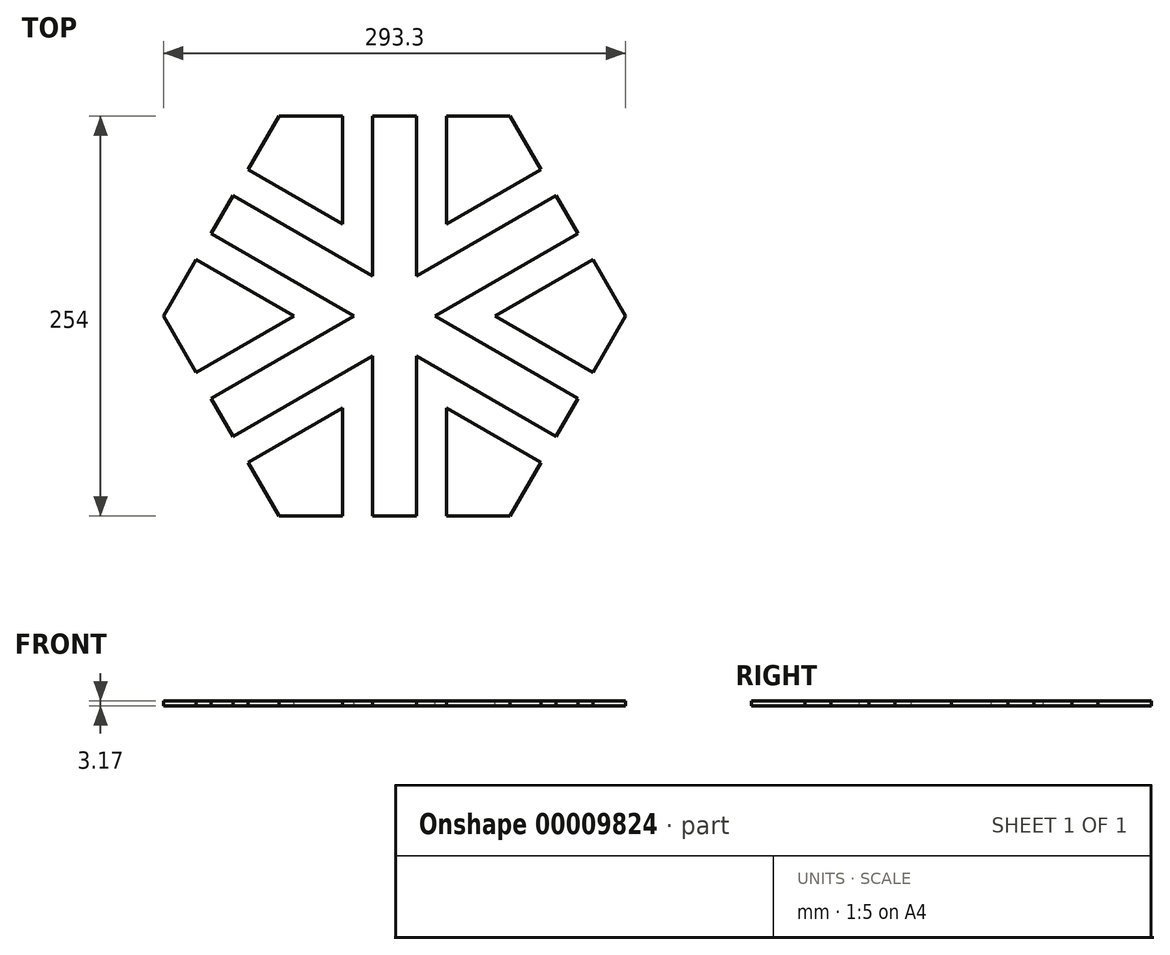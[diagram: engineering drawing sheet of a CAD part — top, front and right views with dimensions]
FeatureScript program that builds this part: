
annotation { "Feature Type Name" : "Feature", "Feature Type Description" : "" }
export const myFeature = defineFeature(function(context is Context, id is Id, definition is map)
    precondition{}
    {
        {
            var Q0;
            Q0=qCreatedBy(makeId("Top.planeOp"),FACE);
            var sketch = newSketch(context, id + "F0", { "sketchPlane" : qUnion([Q0])});
            skCircle(sketch, "E0.cCircle", {"center": v(0, 0) * mm, "radius": 127 * mm, "construction": true});
            skLineSegment(sketch, "E0.0", {"start": v(-73.32, 127) * mm, "end": v(73.32, 127) * mm});
            skLineSegment(sketch, "E0.1", {"start": v(73.32, 127) * mm, "end": v(146.65, 0) * mm});
            skLineSegment(sketch, "E0.2", {"start": v(146.65, 0) * mm, "end": v(73.32, -127) * mm});
            skLineSegment(sketch, "E0.3", {"start": v(73.32, -127) * mm, "end": v(-73.32, -127) * mm});
            skLineSegment(sketch, "E0.4", {"start": v(-73.32, -127) * mm, "end": v(-146.65, 0) * mm});
            skLineSegment(sketch, "E0.5", {"start": v(-146.65, 0) * mm, "end": v(-73.32, 127) * mm});
            skPoint(sketch, "E0.0.midPoint", {"position": v(0, 127) * mm});
            skSolve(sketch);
        }
        {
            var Q0;
            Q0=makeQuery(id+"F0.imprint","IMPRINT",FACE,{"disambiguationData":[TD([[makeQuery(id+"F0.imprint","IMPRINT",EDGE,{"derivedFrom":sQuery(id+"F0.wireOp",EDGE,"E0.0")}),-1.0]])]});
            extrude(context, id + "F1", {"entities" : qUnion([Q0]), "depth" : 3.17 * mm});
        }
        {
            var Q0;
            Q0=makeQuery(id+"F1.opExtrude","CAP_FACE",FACE,{"disambiguationData":[OSD([sQuery(id+"F0.wireOp",EDGE,"E0.0"),sQuery(id+"F0.wireOp",EDGE,"E0.1"),sQuery(id+"F0.wireOp",EDGE,"E0.2"),sQuery(id+"F0.wireOp",EDGE,"E0.3"),sQuery(id+"F0.wireOp",EDGE,"E0.4"),sQuery(id+"F0.wireOp",EDGE,"E0.5")])],"isStart":false});
            var sketch = newSketch(context, id + "F2", { "sketchPlane" : qUnion([Q0])});
            skLineSegment(sketch, "E1", {"start": v(13.97, 127) * mm, "end": v(13.97, 25.4) * mm});
            skLineSegment(sketch, "E2", {"start": v(33.02, 58.4) * mm, "end": v(33.02, 127) * mm});
            skLineSegment(sketch, "E3", {"start": v(13.97, 127) * mm, "end": v(33.02, 127) * mm});
            skLineSegment(sketch, "E4", {"start": v(-13.97, 127) * mm, "end": v(-13.97, 25.4) * mm});
            skLineSegment(sketch, "E5", {"start": v(-13.97, 25.4) * mm, "end": v(-33.02, 58.4) * mm});
            skLineSegment(sketch, "E6", {"start": v(-33.02, 58.4) * mm, "end": v(-33.02, 127) * mm});
            skLineSegment(sketch, "E7", {"start": v(-33.02, 127) * mm, "end": v(-13.97, 127) * mm});
            skPoint(sketch, "E8", {"position": v(0, 18.66) * mm});
            skLineSegment(sketch, "E9", {"start": v(-13.97, -127) * mm, "end": v(-13.97, -25.4) * mm});
            skLineSegment(sketch, "E10", {"start": v(13.97, -127) * mm, "end": v(13.97, -25.4) * mm});
            skLineSegment(sketch, "E11", {"start": v(-13.97, -25.4) * mm, "end": v(-33.02, -58.4) * mm});
            skLineSegment(sketch, "E12", {"start": v(13.97, -25.4) * mm, "end": v(33.02, -58.4) * mm});
            skLineSegment(sketch, "E13", {"start": v(-33.02, -127) * mm, "end": v(-33.02, -58.4) * mm});
            skLineSegment(sketch, "E14", {"start": v(33.02, -127) * mm, "end": v(33.02, -58.4) * mm});
            skLineSegment(sketch, "E15", {"start": v(33.02, -58.4) * mm, "end": v(92.95, -93) * mm});
            skLineSegment(sketch, "E16", {"start": v(13.97, -25.4) * mm, "end": v(102.48, -76.5) * mm});
            skLineSegment(sketch, "E17", {"start": v(-13.97, -25.4) * mm, "end": v(-102.48, -76.5) * mm});
            skLineSegment(sketch, "E18", {"start": v(-33.02, -58.4) * mm, "end": v(-92.95, -93) * mm});
            skLineSegment(sketch, "E19", {"start": v(-13.97, 25.4) * mm, "end": v(-102.48, 76.5) * mm});
            skLineSegment(sketch, "E20", {"start": v(-33.02, 58.4) * mm, "end": v(-92.95, 93) * mm});
            skLineSegment(sketch, "E21", {"start": v(-125.97, -35.8) * mm, "end": v(-63.96, 0) * mm});
            skLineSegment(sketch, "E22", {"start": v(-116.45, -52.3) * mm, "end": v(-25.86, 0) * mm});
            skLineSegment(sketch, "E23", {"start": v(-125.97, 35.8) * mm, "end": v(-63.96, 0) * mm});
            skLineSegment(sketch, "E24", {"start": v(-116.45, 52.3) * mm, "end": v(-25.86, 0) * mm});
            skLineSegment(sketch, "E25", {"start": v(-63.96, 0) * mm, "end": v(-25.86, 0) * mm});
            skLineSegment(sketch, "E26", {"start": v(125.97, -35.8) * mm, "end": v(63.96, 0) * mm});
            skLineSegment(sketch, "E27", {"start": v(116.45, -52.3) * mm, "end": v(25.86, 0) * mm});
            skLineSegment(sketch, "E28", {"start": v(125.97, 35.8) * mm, "end": v(63.96, 0) * mm});
            skLineSegment(sketch, "E29", {"start": v(116.45, 52.3) * mm, "end": v(25.86, 0) * mm});
            skLineSegment(sketch, "E30", {"start": v(25.86, 0) * mm, "end": v(63.96, 0) * mm});
            skLineSegment(sketch, "E31", {"start": v(13.97, 25.4) * mm, "end": v(33.02, 58.4) * mm});
            skLineSegment(sketch, "E32", {"start": v(33.02, 58.4) * mm, "end": v(92.95, 93) * mm});
            skLineSegment(sketch, "E33", {"start": v(13.97, 25.4) * mm, "end": v(102.48, 76.5) * mm});
            skSolve(sketch);
        }
        {
            var Q0;
            Q0=makeQuery(id+"F2.imprint","IMPRINT",FACE,{"disambiguationData":[TD([[makeQuery(id+"F2.imprint","IMPRINT",EDGE,{"derivedFrom":sQuery(id+"F2.wireOp",EDGE,"E4")}),-1.0]])]});
            var Q1;
            Q1=makeQuery(id+"F2.imprint","IMPRINT",FACE,{"disambiguationData":[TD([[makeQuery(id+"F2.imprint","IMPRINT",EDGE,{"derivedFrom":sQuery(id+"F2.wireOp",EDGE,"E1")}),1.0]])]});
            var Q2;
            Q2=makeQuery(id+"F2.imprint","IMPRINT",FACE,{"disambiguationData":[TD([[makeQuery(id+"F2.imprint","IMPRINT",EDGE,{"derivedFrom":sQuery(id+"F2.wireOp",EDGE,"97fdafe7-2def-440a-8930-caca40e22c30")}),-1.0]])]});
            var Q3;
            Q3=makeQuery(id+"F2.imprint","IMPRINT",FACE,{"disambiguationData":[TD([[makeQuery(id+"F2.imprint","IMPRINT",EDGE,{"derivedFrom":sQuery(id+"F2.wireOp",EDGE,"09cba625-7b20-47fa-ac99-ce42a038881a")}),1.0]])]});
            var Q4;
            Q4=makeQuery(id+"F2.imprint","IMPRINT",FACE,{"disambiguationData":[TD([[makeQuery(id+"F2.imprint","IMPRINT",EDGE,{"derivedFrom":sQuery(id+"F2.wireOp",EDGE,"E5")}),1.0]])]});
            var Q5;
            {var subQ2=sQuery(id+"F2.wireOp",EDGE,"E23");Q5=makeQuery(id+"F2.imprint","IMPRINT",FACE,{"disambiguationData":[TD([[makeQuery(id+"F2.imprint","IMPRINT",EDGE,{"derivedFrom":subQ2}),1.0]])]});}
            var Q6;
            {var subQ2=sQuery(id+"F2.wireOp",EDGE,"E21");Q6=makeQuery(id+"F2.imprint","IMPRINT",FACE,{"disambiguationData":[TD([[makeQuery(id+"F2.imprint","IMPRINT",EDGE,{"derivedFrom":subQ2}),-1.0]])]});}
            var Q7;
            Q7=makeQuery(id+"F2.imprint","IMPRINT",FACE,{"disambiguationData":[TD([[makeQuery(id+"F2.imprint","IMPRINT",EDGE,{"derivedFrom":sQuery(id+"F2.wireOp",EDGE,"E11")}),-1.0]])]});
            var Q8;
            {var subQ2=sQuery(id+"F2.wireOp",EDGE,"E9");Q8=makeQuery(id+"F2.imprint","IMPRINT",FACE,{"disambiguationData":[TD([[makeQuery(id+"F2.imprint","IMPRINT",EDGE,{"derivedFrom":subQ2}),1.0]])]});}
            var Q9;
            {var subQ2=sQuery(id+"F2.wireOp",EDGE,"E10");Q9=makeQuery(id+"F2.imprint","IMPRINT",FACE,{"disambiguationData":[TD([[makeQuery(id+"F2.imprint","IMPRINT",EDGE,{"derivedFrom":subQ2}),-1.0]])]});}
            var Q10;
            Q10=makeQuery(id+"F2.imprint","IMPRINT",FACE,{"disambiguationData":[TD([[makeQuery(id+"F2.imprint","IMPRINT",EDGE,{"derivedFrom":sQuery(id+"F2.wireOp",EDGE,"E12")}),1.0]])]});
            var Q11;
            {var subQ2=sQuery(id+"F2.wireOp",EDGE,"E26");Q11=makeQuery(id+"F2.imprint","IMPRINT",FACE,{"disambiguationData":[TD([[makeQuery(id+"F2.imprint","IMPRINT",EDGE,{"derivedFrom":subQ2}),1.0]])]});}
            var Q12;
            {var subQ2=sQuery(id+"F2.wireOp",EDGE,"E28");Q12=makeQuery(id+"F2.imprint","IMPRINT",FACE,{"disambiguationData":[TD([[makeQuery(id+"F2.imprint","IMPRINT",EDGE,{"derivedFrom":subQ2}),-1.0]])]});}
            var Q13;
            Q13=makeQuery(id+"F2.imprint","IMPRINT",FACE,{"disambiguationData":[TD([[makeQuery(id+"F2.imprint","IMPRINT",EDGE,{"derivedFrom":sQuery(id+"F2.wireOp",EDGE,"E31")}),-1.0]])]});
            var Q14;
            Q14=makeQuery(id+"F1.opExtrude","CAP_FACE",FACE,{"disambiguationData":[OSD([sQuery(id+"F0.wireOp",EDGE,"E0.0"),sQuery(id+"F0.wireOp",EDGE,"E0.1"),sQuery(id+"F0.wireOp",EDGE,"E0.2"),sQuery(id+"F0.wireOp",EDGE,"E0.3"),sQuery(id+"F0.wireOp",EDGE,"E0.4"),sQuery(id+"F0.wireOp",EDGE,"E0.5")])],"isStart":true});
            extrude(context, id + "F3", {"entities" : qUnion([Q0, Q1, Q2, Q3, Q4, Q5, Q6, Q7, Q8, Q9, Q10, Q11, Q12, Q13]), "operationType" : NewBodyOperationType.REMOVE, "endBound" : BoundingType.UP_TO_SURFACE, "oppositeDirection" : true, "endBoundEntityFace" : qUnion([Q14]), "depth" : 25.4 * mm});
        }
    });
